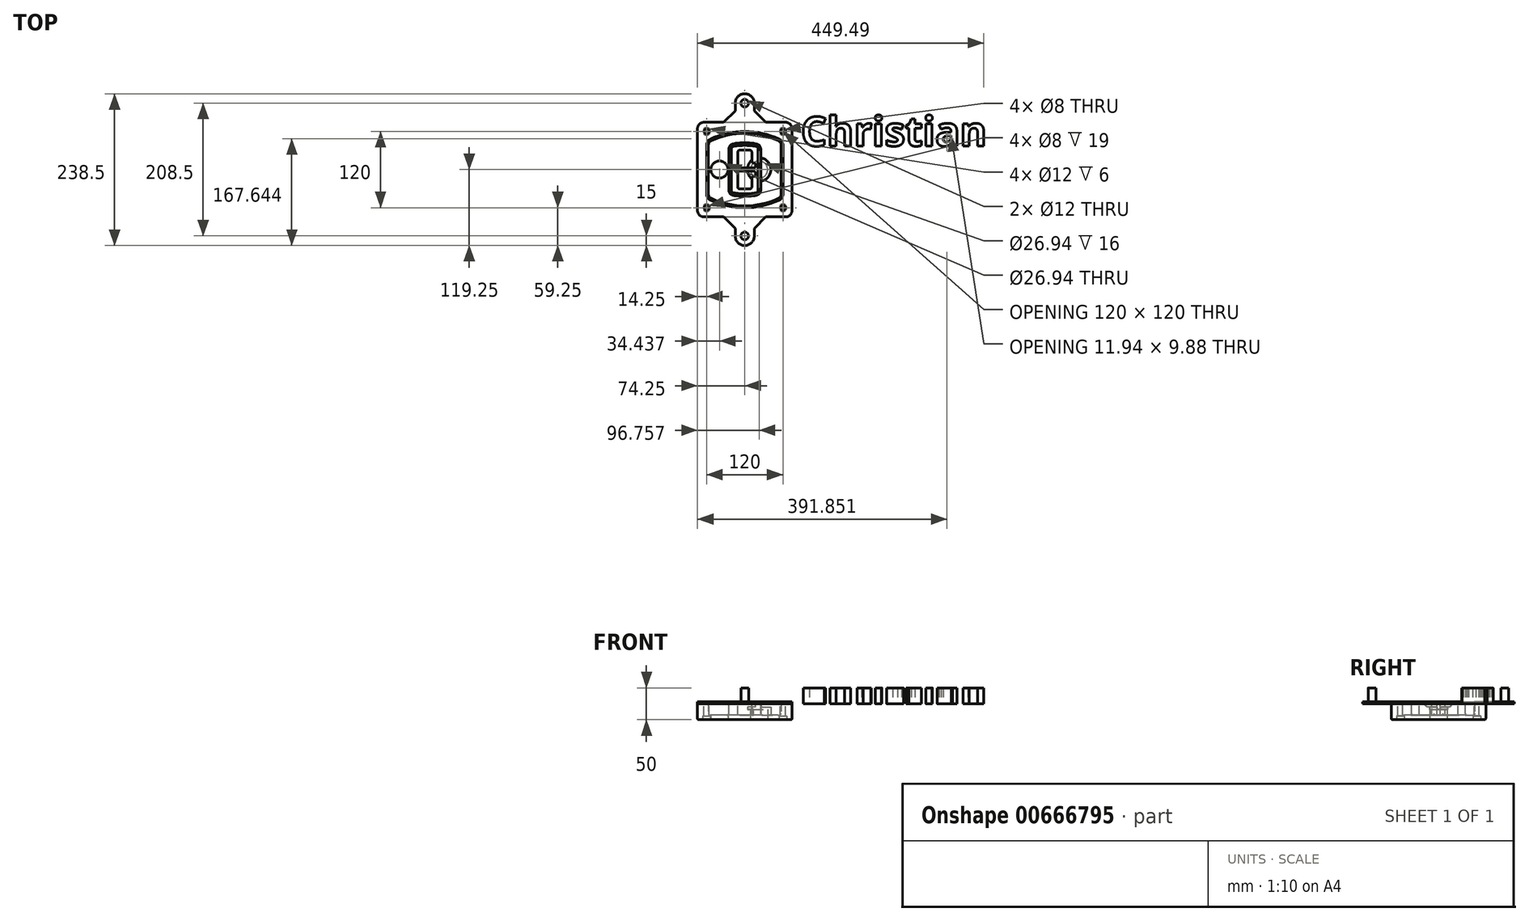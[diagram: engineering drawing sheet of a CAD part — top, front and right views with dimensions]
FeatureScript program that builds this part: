
annotation { "Feature Type Name" : "Feature", "Feature Type Description" : "" }
export const myFeature = defineFeature(function(context is Context, id is Id, definition is map)
    precondition{}
    {
        {
            var Q0;
            Q0=qCreatedBy(makeId("Top.planeOp"),FACE);
            var sketch = newSketch(context, id + "F0", { "sketchPlane" : qUnion([Q0])});
            skPoint(sketch, "E0.rect.middle", {"position": v(0, 0) * mm});
            skLineSegment(sketch, "E1.bottom", {"start": v(-64.25, -74.25) * mm, "end": v(64.25, -74.25) * mm});
            skLineSegment(sketch, "E1.top", {"start": v(-64.25, 74.25) * mm, "end": v(64.25, 74.25) * mm});
            skLineSegment(sketch, "E1.left", {"start": v(-74.25, -64.25) * mm, "end": v(-74.25, 64.25) * mm});
            skLineSegment(sketch, "E1.right", {"start": v(74.25, -64.25) * mm, "end": v(74.25, 64.25) * mm});
            skLineSegment(sketch, "E2", {"start": v(-74.25, 74.25) * mm, "end": v(74.25, -74.25) * mm, "construction": true});
            skLineSegment(sketch, "E3", {"start": v(74.25, 74.25) * mm, "end": v(-74.25, -74.25) * mm, "construction": true});
            skCircle(sketch, "E4", {"center": v(-60, 60) * mm, "radius": 4 * mm});
            skCircle(sketch, "E5", {"center": v(60, 60) * mm, "radius": 4 * mm});
            skCircle(sketch, "E6", {"center": v(60, -60) * mm, "radius": 4 * mm});
            skCircle(sketch, "E7", {"center": v(-60, -60) * mm, "radius": 4 * mm});
            skLineSegment(sketch, "E8", {"start": v(-60, 60) * mm, "end": v(60, 60) * mm, "construction": true});
            skLineSegment(sketch, "E9", {"start": v(60, 60) * mm, "end": v(60, -60) * mm, "construction": true});
            skLineSegment(sketch, "E10", {"start": v(60, -60) * mm, "end": v(-60, -60) * mm, "construction": true});
            skLineSegment(sketch, "E11", {"start": v(-60, -60) * mm, "end": v(-60, 60) * mm, "construction": true});
            skLineSegment(sketch, "E12", {"start": v(-60, 38.83) * mm, "end": v(-60, -38.83) * mm});
            skLineSegment(sketch, "E13", {"start": v(60, 38.83) * mm, "end": v(60, -38.83) * mm});
            skArc(sketch, "E14", {"start": v(54.26, 47.88) * mm, "mid": v(0, 60) * mm, "end": v(-54.26, 47.88) * mm});
            skArc(sketch, "E15", {"start": v(-54.26, -47.88) * mm, "mid": v(0, -60) * mm, "end": v(54.26, -47.88) * mm});
            skLineSegment(sketch, "E16", {"start": v(-60, 0) * mm, "end": v(60, 0) * mm, "construction": true});
            skPoint(sketch, "E17.visualSharp", {"position": v(-60, -45) * mm});
            skArc(sketch, "E17.filletArc", {"start": v(-60, -38.83) * mm, "mid": v(-58.44, -44.2) * mm, "end": v(-54.26, -47.88) * mm});
            skPoint(sketch, "E18.visualSharp", {"position": v(-60, 45) * mm});
            skArc(sketch, "E18.filletArc", {"start": v(-54.26, 47.88) * mm, "mid": v(-58.44, 44.2) * mm, "end": v(-60, 38.83) * mm});
            skPoint(sketch, "E19.visualSharp", {"position": v(60, 45) * mm});
            skArc(sketch, "E19.filletArc", {"start": v(60, 38.83) * mm, "mid": v(58.44, 44.2) * mm, "end": v(54.26, 47.88) * mm});
            skPoint(sketch, "E20.visualSharp", {"position": v(60, -45) * mm});
            skArc(sketch, "E20.filletArc", {"start": v(54.26, -47.88) * mm, "mid": v(58.44, -44.2) * mm, "end": v(60, -38.83) * mm});
            skPoint(sketch, "E21.visualSharp", {"position": v(-74.25, 74.25) * mm});
            skArc(sketch, "E21.filletArc", {"start": v(-64.25, 74.25) * mm, "mid": v(-71.32, 71.32) * mm, "end": v(-74.25, 64.25) * mm});
            skPoint(sketch, "E22.visualSharp", {"position": v(74.25, 74.25) * mm});
            skArc(sketch, "E22.filletArc", {"start": v(74.25, 64.25) * mm, "mid": v(71.32, 71.32) * mm, "end": v(64.25, 74.25) * mm});
            skPoint(sketch, "E23.visualSharp", {"position": v(74.25, -74.25) * mm});
            skArc(sketch, "E23.filletArc", {"start": v(64.25, -74.25) * mm, "mid": v(71.32, -71.32) * mm, "end": v(74.25, -64.25) * mm});
            skPoint(sketch, "E24.visualSharp", {"position": v(-74.25, -74.25) * mm});
            skArc(sketch, "E24.filletArc", {"start": v(-74.25, -64.25) * mm, "mid": v(-71.32, -71.32) * mm, "end": v(-64.25, -74.25) * mm});
            skArc(sketch, "E25.0", {"start": v(57, 38.83) * mm, "mid": v(55.9, 42.58) * mm, "end": v(52.98, 45.17) * mm});
            skLineSegment(sketch, "E25.1", {"start": v(57, 38.83) * mm, "end": v(57, -38.83) * mm});
            skArc(sketch, "E25.2", {"start": v(52.98, -45.17) * mm, "mid": v(55.9, -42.58) * mm, "end": v(57, -38.83) * mm});
            skArc(sketch, "E25.3", {"start": v(-52.98, -45.17) * mm, "mid": v(0, -57) * mm, "end": v(52.98, -45.17) * mm});
            skArc(sketch, "E25.4", {"start": v(-57, -38.83) * mm, "mid": v(-55.9, -42.58) * mm, "end": v(-52.98, -45.17) * mm});
            skArc(sketch, "E25.5", {"start": v(52.98, 45.17) * mm, "mid": v(0, 57) * mm, "end": v(-52.98, 45.17) * mm});
            skLineSegment(sketch, "E25.6", {"start": v(-57, 38.83) * mm, "end": v(-57, -38.83) * mm});
            skArc(sketch, "E25.7", {"start": v(-52.98, 45.17) * mm, "mid": v(-55.9, 42.58) * mm, "end": v(-57, 38.83) * mm});
            skArc(sketch, "E26.0", {"start": v(-55.96, 51.5) * mm, "mid": v(-61.82, 46.33) * mm, "end": v(-64, 38.83) * mm});
            skArc(sketch, "E26.1", {"start": v(55.96, 51.5) * mm, "mid": v(0, 64) * mm, "end": v(-55.96, 51.5) * mm});
            skArc(sketch, "E26.2", {"start": v(64, 38.83) * mm, "mid": v(61.82, 46.33) * mm, "end": v(55.96, 51.5) * mm});
            skLineSegment(sketch, "E26.3", {"start": v(64, 38.83) * mm, "end": v(64, -38.83) * mm});
            skArc(sketch, "E26.4", {"start": v(55.96, -51.5) * mm, "mid": v(61.82, -46.33) * mm, "end": v(64, -38.83) * mm});
            skLineSegment(sketch, "E26.5", {"start": v(-64, 38.83) * mm, "end": v(-64, -38.83) * mm});
            skArc(sketch, "E26.6", {"start": v(-55.96, -51.5) * mm, "mid": v(0, -64) * mm, "end": v(55.96, -51.5) * mm});
            skArc(sketch, "E26.7", {"start": v(-64, -38.83) * mm, "mid": v(-61.82, -46.33) * mm, "end": v(-55.96, -51.5) * mm});
            skSolve(sketch);
        }
        {
            var Q0;
            Q0=makeQuery(id+"F0.imprint","IMPRINT",FACE,{"disambiguationData":[TD([[makeQuery(id+"F0.imprint","IMPRINT",EDGE,{"derivedFrom":sQuery(id+"F0.wireOp",EDGE,"E1.bottom")}),1.0]])]});
            var Q1;
            Q1=makeQuery(id+"F0.imprint","IMPRINT",FACE,{"disambiguationData":[TD([[makeQuery(id+"F0.imprint","IMPRINT",EDGE,{"derivedFrom":sQuery(id+"F0.wireOp",EDGE,"E12")}),1.0]])]});
            var Q2;
            Q2=makeQuery(id+"F0.imprint","IMPRINT",FACE,{"disambiguationData":[TD([[makeQuery(id+"F0.imprint","IMPRINT",EDGE,{"derivedFrom":sQuery(id+"F0.wireOp",EDGE,"E25.0")}),1.0]])]});
            var Q3;
            Q3=makeQuery(id+"F0.imprint","IMPRINT",FACE,{"disambiguationData":[TD([[makeQuery(id+"F0.imprint","IMPRINT",EDGE,{"derivedFrom":sQuery(id+"F0.wireOp",EDGE,"E12")}),-1.0]])]});
            extrude(context, id + "F1", {"entities" : qUnion([Q0, Q1, Q2, Q3]), "oppositeDirection" : true, "depth" : 25 * mm});
        }
        {
            var Q0;
            Q0=makeQuery(id+"F0.imprint","IMPRINT",FACE,{"disambiguationData":[TD([[makeQuery(id+"F0.imprint","IMPRINT",EDGE,{"derivedFrom":sQuery(id+"F0.wireOp",EDGE,"E12")}),1.0]])]});
            extrude(context, id + "F2", {"entities" : qUnion([Q0]), "operationType" : NewBodyOperationType.ADD, "depth" : 3 * mm});
        }
        {
            var Q0;
            Q0=makeQuery(id+"F0.imprint","IMPRINT",FACE,{"disambiguationData":[TD([[makeQuery(id+"F0.imprint","IMPRINT",EDGE,{"derivedFrom":sQuery(id+"F0.wireOp",EDGE,"E25.0")}),1.0]])]});
            extrude(context, id + "F3", {"entities" : qUnion([Q0]), "operationType" : NewBodyOperationType.REMOVE, "oppositeDirection" : true, "depth" : 18 * mm});
        }
        {
            var Q0;
            Q0=makeQuery(id+"F2.opExtrude","CAP_FACE",FACE,{"disambiguationData":[OSD([sQuery(id+"F0.wireOp",EDGE,"E12"),sQuery(id+"F0.wireOp",EDGE,"E13"),sQuery(id+"F0.wireOp",EDGE,"E14"),sQuery(id+"F0.wireOp",EDGE,"E15"),sQuery(id+"F0.wireOp",EDGE,"E17.filletArc"),sQuery(id+"F0.wireOp",EDGE,"E18.filletArc"),sQuery(id+"F0.wireOp",EDGE,"E19.filletArc"),sQuery(id+"F0.wireOp",EDGE,"E20.filletArc"),sQuery(id+"F0.wireOp",EDGE,"E25.0"),sQuery(id+"F0.wireOp",EDGE,"E25.1"),sQuery(id+"F0.wireOp",EDGE,"E25.2"),sQuery(id+"F0.wireOp",EDGE,"E25.3"),sQuery(id+"F0.wireOp",EDGE,"E25.4"),sQuery(id+"F0.wireOp",EDGE,"E25.5"),sQuery(id+"F0.wireOp",EDGE,"E25.6"),sQuery(id+"F0.wireOp",EDGE,"E25.7")])],"isStart":false});
            var sketch = newSketch(context, id + "F4", { "sketchPlane" : qUnion([Q0])});
            skArc(sketch, "E27.0", {"start": v(-18.34, -40.45) * mm, "mid": v(0, -42) * mm, "end": v(18.34, -40.45) * mm});
            skArc(sketch, "E28.0", {"start": v(18.34, 40.45) * mm, "mid": v(0, 42) * mm, "end": v(-18.34, 40.45) * mm});
            skLineSegment(sketch, "E29", {"start": v(-25, 32.57) * mm, "end": v(-25, -32.57) * mm});
            skLineSegment(sketch, "E30", {"start": v(25, 32.57) * mm, "end": v(25, -32.57) * mm});
            skLineSegment(sketch, "E31", {"start": v(-25, 39.1) * mm, "end": v(25, 39.1) * mm, "construction": true});
            skLineSegment(sketch, "E32", {"start": v(-25, -39.1) * mm, "end": v(25, -39.1) * mm, "construction": true});
            skPoint(sketch, "E33.visualSharp", {"position": v(-25, 39.1) * mm});
            skArc(sketch, "E33.filletArc", {"start": v(-18.34, 40.45) * mm, "mid": v(-23.11, 37.73) * mm, "end": v(-25, 32.57) * mm});
            skPoint(sketch, "E34.visualSharp", {"position": v(25, 39.1) * mm});
            skArc(sketch, "E34.filletArc", {"start": v(25, 32.57) * mm, "mid": v(23.11, 37.73) * mm, "end": v(18.34, 40.45) * mm});
            skPoint(sketch, "E35.visualSharp", {"position": v(25, -39.1) * mm});
            skArc(sketch, "E35.filletArc", {"start": v(18.34, -40.45) * mm, "mid": v(23.11, -37.73) * mm, "end": v(25, -32.57) * mm});
            skPoint(sketch, "E36.visualSharp", {"position": v(-25, -39.1) * mm});
            skArc(sketch, "E36.filletArc", {"start": v(-25, -32.57) * mm, "mid": v(-23.11, -37.73) * mm, "end": v(-18.34, -40.45) * mm});
            skArc(sketch, "E37.0", {"start": v(52.98, 45.17) * mm, "mid": v(0, 57) * mm, "end": v(-52.98, 45.17) * mm});
            skArc(sketch, "E37.1", {"start": v(-52.98, 45.17) * mm, "mid": v(-55.9, 42.58) * mm, "end": v(-57, 38.83) * mm});
            skLineSegment(sketch, "E37.2", {"start": v(-57, 38.83) * mm, "end": v(-57, -38.83) * mm});
            skArc(sketch, "E37.3", {"start": v(-57, -38.83) * mm, "mid": v(-55.9, -42.58) * mm, "end": v(-52.98, -45.17) * mm});
            skArc(sketch, "E37.4", {"start": v(-52.98, -45.17) * mm, "mid": v(0, -57) * mm, "end": v(52.98, -45.17) * mm});
            skArc(sketch, "E37.5", {"start": v(52.98, -45.17) * mm, "mid": v(55.9, -42.58) * mm, "end": v(57, -38.83) * mm});
            skLineSegment(sketch, "E37.6", {"start": v(57, 38.83) * mm, "end": v(57, -38.83) * mm});
            skArc(sketch, "E37.7", {"start": v(57, 38.83) * mm, "mid": v(55.9, 42.58) * mm, "end": v(52.98, 45.17) * mm});
            skLineSegment(sketch, "E38.0", {"start": v(23, 32.57) * mm, "end": v(23, -32.57) * mm});
            skArc(sketch, "E38.1", {"start": v(18, -38.48) * mm, "mid": v(21.58, -36.44) * mm, "end": v(23, -32.57) * mm});
            skArc(sketch, "E38.2", {"start": v(-18, -38.48) * mm, "mid": v(0, -40) * mm, "end": v(18, -38.48) * mm});
            skArc(sketch, "E38.3", {"start": v(-23, -32.57) * mm, "mid": v(-21.58, -36.44) * mm, "end": v(-18, -38.48) * mm});
            skLineSegment(sketch, "E38.4", {"start": v(-23, 32.57) * mm, "end": v(-23, -32.57) * mm});
            skArc(sketch, "E38.5", {"start": v(23, 32.57) * mm, "mid": v(21.58, 36.44) * mm, "end": v(18, 38.48) * mm});
            skArc(sketch, "E38.6", {"start": v(-18, 38.48) * mm, "mid": v(-21.58, 36.44) * mm, "end": v(-23, 32.57) * mm});
            skArc(sketch, "E38.7", {"start": v(18, 38.48) * mm, "mid": v(0, 40) * mm, "end": v(-18, 38.48) * mm});
            skArc(sketch, "E39.0", {"start": v(21, 32.57) * mm, "mid": v(20.06, 35.15) * mm, "end": v(17.67, 36.5) * mm});
            skLineSegment(sketch, "E39.1", {"start": v(21, 32.57) * mm, "end": v(21, -32.57) * mm});
            skArc(sketch, "E39.2", {"start": v(17.67, -36.5) * mm, "mid": v(20.06, -35.15) * mm, "end": v(21, -32.57) * mm});
            skArc(sketch, "E39.3", {"start": v(-17.67, -36.5) * mm, "mid": v(0, -38) * mm, "end": v(17.67, -36.5) * mm});
            skArc(sketch, "E39.4", {"start": v(-21, -32.57) * mm, "mid": v(-20.06, -35.15) * mm, "end": v(-17.67, -36.5) * mm});
            skArc(sketch, "E39.5", {"start": v(17.67, 36.5) * mm, "mid": v(0, 38) * mm, "end": v(-17.67, 36.5) * mm});
            skLineSegment(sketch, "E39.6", {"start": v(-21, 32.57) * mm, "end": v(-21, -32.57) * mm});
            skArc(sketch, "E39.7", {"start": v(-17.67, 36.5) * mm, "mid": v(-20.06, 35.15) * mm, "end": v(-21, 32.57) * mm});
            skLineSegment(sketch, "E40", {"start": v(-25, 0) * mm, "end": v(25, 0) * mm, "construction": true});
            skLineSegment(sketch, "E41", {"start": v(-11, 5.5) * mm, "end": v(-11, 27.5) * mm});
            skLineSegment(sketch, "E42", {"start": v(-8, 30.5) * mm, "end": v(8, 30.5) * mm});
            skLineSegment(sketch, "E43", {"start": v(11, 27.5) * mm, "end": v(11, 13.5) * mm});
            skLineSegment(sketch, "E44", {"start": v(14, 10.5) * mm, "end": v(14, 10.5) * mm});
            skLineSegment(sketch, "E45", {"start": v(17, 7.5) * mm, "end": v(17, 5.5) * mm});
            skLineSegment(sketch, "E46", {"start": v(14, 2.5) * mm, "end": v(-8, 2.5) * mm});
            skPoint(sketch, "E47.visualSharp", {"position": v(-11, 30.5) * mm});
            skArc(sketch, "E47.filletArc", {"start": v(-8, 30.5) * mm, "mid": v(-10.12, 29.62) * mm, "end": v(-11, 27.5) * mm});
            skPoint(sketch, "E48.visualSharp", {"position": v(11, 30.5) * mm});
            skArc(sketch, "E48.filletArc", {"start": v(11, 27.5) * mm, "mid": v(10.12, 29.62) * mm, "end": v(8, 30.5) * mm});
            skPoint(sketch, "E49.visualSharp", {"position": v(11, 10.5) * mm});
            skArc(sketch, "E49.filletArc", {"start": v(11, 13.5) * mm, "mid": v(11.88, 11.38) * mm, "end": v(14, 10.5) * mm});
            skPoint(sketch, "E50.visualSharp", {"position": v(17, 10.5) * mm});
            skArc(sketch, "E50.filletArc", {"start": v(17, 7.5) * mm, "mid": v(16.12, 9.62) * mm, "end": v(14, 10.5) * mm});
            skPoint(sketch, "E51.visualSharp", {"position": v(17, 2.5) * mm});
            skArc(sketch, "E51.filletArc", {"start": v(14, 2.5) * mm, "mid": v(16.12, 3.38) * mm, "end": v(17, 5.5) * mm});
            skPoint(sketch, "E52.visualSharp", {"position": v(-11, 2.5) * mm});
            skArc(sketch, "E52.filletArc", {"start": v(-11, 5.5) * mm, "mid": v(-10.12, 3.38) * mm, "end": v(-8, 2.5) * mm});
            skLineSegment(sketch, "E53.0.MirrorCS", {"start": v(14, -2.5) * mm, "end": v(-8, -2.5) * mm});
            skArc(sketch, "E54.0.MirrorCS", {"start": v(-11, -5.5) * mm, "mid": v(-10.12, -3.38) * mm, "end": v(-8, -2.5) * mm});
            skLineSegment(sketch, "E55.0.MirrorCS", {"start": v(-11, -5.5) * mm, "end": v(-11, -27.5) * mm});
            skArc(sketch, "E56.0.MirrorCS", {"start": v(-8, -30.5) * mm, "mid": v(-10.12, -29.62) * mm, "end": v(-11, -27.5) * mm});
            skLineSegment(sketch, "E57.0.MirrorCS", {"start": v(-8, -30.5) * mm, "end": v(8, -30.5) * mm});
            skArc(sketch, "E58.0.MirrorCS", {"start": v(11, -27.5) * mm, "mid": v(10.12, -29.62) * mm, "end": v(8, -30.5) * mm});
            skLineSegment(sketch, "E59.0.MirrorCS", {"start": v(11, -27.5) * mm, "end": v(11, -13.5) * mm});
            skArc(sketch, "E60.0.MirrorCS", {"start": v(11, -13.5) * mm, "mid": v(11.88, -11.38) * mm, "end": v(14, -10.5) * mm});
            skArc(sketch, "E61.0.MirrorCS", {"start": v(17, -7.5) * mm, "mid": v(16.12, -9.62) * mm, "end": v(14, -10.5) * mm});
            skLineSegment(sketch, "E62.0.MirrorCS", {"start": v(17, -7.5) * mm, "end": v(17, -5.5) * mm});
            skArc(sketch, "E63.0.MirrorCS", {"start": v(14, -2.5) * mm, "mid": v(16.12, -3.38) * mm, "end": v(17, -5.5) * mm});
            skSolve(sketch);
        }
        {
            var Q0;
            Q0=makeQuery(id+"F4.imprint","IMPRINT",FACE,{"disambiguationData":[TD([[makeQuery(id+"F4.imprint","IMPRINT",EDGE,{"derivedFrom":sQuery(id+"F4.wireOp",EDGE,"E27.0")}),1.0]])]});
            var Q1;
            Q1=makeQuery(id+"F4.imprint","IMPRINT",FACE,{"disambiguationData":[TD([[makeQuery(id+"F4.imprint","IMPRINT",EDGE,{"derivedFrom":sQuery(id+"F4.wireOp",EDGE,"E38.0")}),-1.0]])]});
            var Q2;
            Q2=makeQuery(id+"F4.imprint","IMPRINT",FACE,{"disambiguationData":[TD([[makeQuery(id+"F4.imprint","IMPRINT",EDGE,{"derivedFrom":sQuery(id+"F4.wireOp",EDGE,"E39.0")}),1.0]])]});
            extrude(context, id + "F5", {"entities" : qUnion([Q0, Q1, Q2]), "operationType" : NewBodyOperationType.ADD, "endBound" : BoundingType.UP_TO_NEXT, "oppositeDirection" : true, "depth" : 25 * mm});
        }
        {
            var Q0;
            Q0=makeQuery(id+"F4.imprint","IMPRINT",FACE,{"disambiguationData":[TD([[makeQuery(id+"F4.imprint","IMPRINT",EDGE,{"derivedFrom":sQuery(id+"F4.wireOp",EDGE,"E38.0")}),-1.0]])]});
            extrude(context, id + "F6", {"entities" : qUnion([Q0]), "operationType" : NewBodyOperationType.REMOVE, "oppositeDirection" : true, "depth" : 2 * mm});
        }
        {
            var Q0;
            Q0=makeQuery(id+"F1.opExtrude","CAP_FACE",FACE,{"disambiguationData":[OSD([sQuery(id+"F0.wireOp",EDGE,"E1.bottom"),sQuery(id+"F0.wireOp",EDGE,"E1.top"),sQuery(id+"F0.wireOp",EDGE,"E1.left"),sQuery(id+"F0.wireOp",EDGE,"E1.right"),sQuery(id+"F0.wireOp",EDGE,"E4"),sQuery(id+"F0.wireOp",EDGE,"E5"),sQuery(id+"F0.wireOp",EDGE,"E6"),sQuery(id+"F0.wireOp",EDGE,"E7"),sQuery(id+"F0.wireOp",EDGE,"E21.filletArc"),sQuery(id+"F0.wireOp",EDGE,"E22.filletArc"),sQuery(id+"F0.wireOp",EDGE,"E23.filletArc"),sQuery(id+"F0.wireOp",EDGE,"E24.filletArc")])],"isStart":false});
            var sketch = newSketch(context, id + "F7", { "sketchPlane" : qUnion([Q0])});
            skCircle(sketch, "E64", {"center": v(22.5, 0) * mm, "radius": 13.47 * mm});
            skCircle(sketch, "E65", {"center": v(-39.81, 0) * mm, "radius": 13.47 * mm});
            skLineSegment(sketch, "E66", {"start": v(74.25, 0) * mm, "end": v(-74.25, 0) * mm});
            skCircle(sketch, "E67", {"center": v(22.5, 0) * mm, "radius": 18.47 * mm});
            skCircle(sketch, "E68", {"center": v(60, -60) * mm, "radius": 6 * mm});
            skCircle(sketch, "E69", {"center": v(-60, -60) * mm, "radius": 6 * mm});
            skCircle(sketch, "E70", {"center": v(-60, 60) * mm, "radius": 6 * mm});
            skCircle(sketch, "E71", {"center": v(60, 60) * mm, "radius": 6 * mm});
            skSolve(sketch);
        }
        {
            var Q0;
            {var subQ1=sQuery(id+"F7.wireOp",EDGE,"E66");var subQ4=sQuery(id+"F7.wireOp",EDGE,"E64");var subQ6=makeQuery(id+"F7.imprint","INTERSECT",VERTEX,{"disambiguationData":[OD(0.0)],"derivedFrom":[subQ4,subQ1]});Q0=makeQuery(id+"F7.imprint","IMPRINT",FACE,{"disambiguationData":[TD([[makeQuery(id+"F7.imprint","IMPRINT",EDGE,{"disambiguationData":[TD([[subQ6,-1.0]])],"derivedFrom":subQ4}),-1.0]])]});}
            var Q1;
            {var subQ0=sQuery(id+"F7.wireOp",EDGE,"E66");var subQ1=sQuery(id+"F7.wireOp",EDGE,"E64");var subQ3=makeQuery(id+"F7.imprint","INTERSECT",VERTEX,{"disambiguationData":[OD(0.0)],"derivedFrom":[subQ1,subQ0]});Q1=makeQuery(id+"F7.imprint","IMPRINT",FACE,{"disambiguationData":[TD([[makeQuery(id+"F7.imprint","IMPRINT",EDGE,{"disambiguationData":[TD([[subQ3,-1.0]])],"derivedFrom":subQ1}),1.0]])]});}
            var Q2;
            {var subQ0=sQuery(id+"F7.wireOp",EDGE,"E66");var subQ1=sQuery(id+"F7.wireOp",EDGE,"E64");var subQ3=makeQuery(id+"F7.imprint","INTERSECT",VERTEX,{"disambiguationData":[OD(0.0)],"derivedFrom":[subQ1,subQ0]});Q2=makeQuery(id+"F7.imprint","IMPRINT",FACE,{"disambiguationData":[TD([[makeQuery(id+"F7.imprint","IMPRINT",EDGE,{"disambiguationData":[TD([[subQ3,1.0]])],"derivedFrom":subQ1}),1.0]])]});}
            var Q3;
            {var subQ1=sQuery(id+"F7.wireOp",EDGE,"E66");var subQ4=sQuery(id+"F7.wireOp",EDGE,"E64");var subQ6=makeQuery(id+"F7.imprint","INTERSECT",VERTEX,{"disambiguationData":[OD(0.0)],"derivedFrom":[subQ4,subQ1]});Q3=makeQuery(id+"F7.imprint","IMPRINT",FACE,{"disambiguationData":[TD([[makeQuery(id+"F7.imprint","IMPRINT",EDGE,{"disambiguationData":[TD([[subQ6,1.0]])],"derivedFrom":subQ4}),-1.0]])]});}
            extrude(context, id + "F8", {"entities" : qUnion([Q0, Q1, Q2, Q3]), "operationType" : NewBodyOperationType.ADD, "oppositeDirection" : true, "depth" : 20 * mm});
        }
        {
            var Q0;
            {var subQ0=sQuery(id+"F7.wireOp",EDGE,"E66");var subQ1=sQuery(id+"F7.wireOp",EDGE,"E64");var subQ3=makeQuery(id+"F7.imprint","INTERSECT",VERTEX,{"disambiguationData":[OD(0.0)],"derivedFrom":[subQ1,subQ0]});Q0=makeQuery(id+"F7.imprint","IMPRINT",FACE,{"disambiguationData":[TD([[makeQuery(id+"F7.imprint","IMPRINT",EDGE,{"disambiguationData":[TD([[subQ3,-1.0]])],"derivedFrom":subQ1}),1.0]])]});}
            var Q1;
            {var subQ0=sQuery(id+"F7.wireOp",EDGE,"E66");var subQ1=sQuery(id+"F7.wireOp",EDGE,"E64");var subQ3=makeQuery(id+"F7.imprint","INTERSECT",VERTEX,{"disambiguationData":[OD(0.0)],"derivedFrom":[subQ1,subQ0]});Q1=makeQuery(id+"F7.imprint","IMPRINT",FACE,{"disambiguationData":[TD([[makeQuery(id+"F7.imprint","IMPRINT",EDGE,{"disambiguationData":[TD([[subQ3,1.0]])],"derivedFrom":subQ1}),1.0]])]});}
            extrude(context, id + "F9", {"entities" : qUnion([Q0, Q1]), "operationType" : NewBodyOperationType.REMOVE, "oppositeDirection" : true, "depth" : 16 * mm});
        }
        {
            var Q0;
            {var subQ0=sQuery(id+"F7.wireOp",EDGE,"E66");var subQ1=sQuery(id+"F7.wireOp",EDGE,"E65");var subQ3=makeQuery(id+"F7.imprint","INTERSECT",VERTEX,{"disambiguationData":[OD(0.0)],"derivedFrom":[subQ1,subQ0]});Q0=makeQuery(id+"F7.imprint","IMPRINT",FACE,{"disambiguationData":[TD([[makeQuery(id+"F7.imprint","IMPRINT",EDGE,{"disambiguationData":[TD([[subQ3,-1.0]])],"derivedFrom":subQ1}),1.0]])]});}
            var Q1;
            {var subQ0=sQuery(id+"F7.wireOp",EDGE,"E66");var subQ1=sQuery(id+"F7.wireOp",EDGE,"E65");var subQ3=makeQuery(id+"F7.imprint","INTERSECT",VERTEX,{"disambiguationData":[OD(0.0)],"derivedFrom":[subQ1,subQ0]});Q1=makeQuery(id+"F7.imprint","IMPRINT",FACE,{"disambiguationData":[TD([[makeQuery(id+"F7.imprint","IMPRINT",EDGE,{"disambiguationData":[TD([[subQ3,1.0]])],"derivedFrom":subQ1}),1.0]])]});}
            extrude(context, id + "F10", {"entities" : qUnion([Q0, Q1]), "operationType" : NewBodyOperationType.REMOVE, "oppositeDirection" : true, "depth" : 25 * mm});
        }
        {
            var Q0;
            Q0=makeQuery(id+"F7.imprint","IMPRINT",FACE,{"disambiguationData":[TD([[makeQuery(id+"F7.imprint","IMPRINT",EDGE,{"derivedFrom":sQuery(id+"F7.wireOp",EDGE,"E68")}),1.0]])]});
            var Q1;
            Q1=makeQuery(id+"F7.imprint","IMPRINT",FACE,{"disambiguationData":[TD([[makeQuery(id+"F7.imprint","IMPRINT",EDGE,{"derivedFrom":makeQuery(id+"F1.opExtrude","CAP_EDGE",EDGE,{"disambiguationData":[OSD([sQuery(id+"F0.wireOp",EDGE,"E5")])],"isStart":false})}),-1.0]])]});
            var Q2;
            Q2=makeQuery(id+"F7.imprint","IMPRINT",FACE,{"disambiguationData":[TD([[makeQuery(id+"F7.imprint","IMPRINT",EDGE,{"derivedFrom":sQuery(id+"F7.wireOp",EDGE,"E69")}),1.0]])]});
            var Q3;
            Q3=makeQuery(id+"F7.imprint","IMPRINT",FACE,{"disambiguationData":[TD([[makeQuery(id+"F7.imprint","IMPRINT",EDGE,{"derivedFrom":makeQuery(id+"F1.opExtrude","CAP_EDGE",EDGE,{"disambiguationData":[OSD([sQuery(id+"F0.wireOp",EDGE,"E4")])],"isStart":false})}),-1.0]])]});
            var Q4;
            Q4=makeQuery(id+"F7.imprint","IMPRINT",FACE,{"disambiguationData":[TD([[makeQuery(id+"F7.imprint","IMPRINT",EDGE,{"derivedFrom":sQuery(id+"F7.wireOp",EDGE,"E70")}),1.0]])]});
            var Q5;
            Q5=makeQuery(id+"F7.imprint","IMPRINT",FACE,{"disambiguationData":[TD([[makeQuery(id+"F7.imprint","IMPRINT",EDGE,{"derivedFrom":makeQuery(id+"F1.opExtrude","CAP_EDGE",EDGE,{"disambiguationData":[OSD([sQuery(id+"F0.wireOp",EDGE,"E7")])],"isStart":false})}),-1.0]])]});
            var Q6;
            Q6=makeQuery(id+"F7.imprint","IMPRINT",FACE,{"disambiguationData":[TD([[makeQuery(id+"F7.imprint","IMPRINT",EDGE,{"derivedFrom":sQuery(id+"F7.wireOp",EDGE,"E71")}),1.0]])]});
            var Q7;
            Q7=makeQuery(id+"F7.imprint","IMPRINT",FACE,{"disambiguationData":[TD([[makeQuery(id+"F7.imprint","IMPRINT",EDGE,{"derivedFrom":makeQuery(id+"F1.opExtrude","CAP_EDGE",EDGE,{"disambiguationData":[OSD([sQuery(id+"F0.wireOp",EDGE,"E6")])],"isStart":false})}),-1.0]])]});
            extrude(context, id + "F11", {"entities" : qUnion([Q0, Q1, Q2, Q3, Q4, Q5, Q6, Q7]), "operationType" : NewBodyOperationType.REMOVE, "oppositeDirection" : true, "depth" : 6 * mm});
        }
        {
            var Q0;
            Q0=makeQuery(id+"F9.boolean.opBoolean","COPY",FACE,{"derivedFrom":makeQuery(id+"F9.opExtrude","CAP_FACE",FACE,{"disambiguationData":[OSD([sQuery(id+"F7.wireOp",EDGE,"E64")])],"isStart":false})});
            var sketch = newSketch(context, id + "F12", { "sketchPlane" : qUnion([Q0])});
            skArc(sketch, "E72.0", {"start": v(11, 14.45) * mm, "mid": v(6.45, 9.13) * mm, "end": v(4.2, 2.5) * mm});
            skArc(sketch, "E72.1", {"start": v(4.2, -2.5) * mm, "mid": v(6.45, -9.13) * mm, "end": v(11, -14.45) * mm});
            skLineSegment(sketch, "E73", {"start": v(4.2, -2.5) * mm, "end": v(14, -2.5) * mm});
            skLineSegment(sketch, "E74.0", {"start": v(14, 2.5) * mm, "end": v(4.2, 2.5) * mm});
            skArc(sketch, "E74.1", {"start": v(14, 2.5) * mm, "mid": v(16.12, 3.38) * mm, "end": v(17, 5.5) * mm});
            skLineSegment(sketch, "E74.2", {"start": v(17, 7.5) * mm, "end": v(17, 5.5) * mm});
            skArc(sketch, "E74.3", {"start": v(17, 7.5) * mm, "mid": v(16.12, 9.62) * mm, "end": v(14, 10.5) * mm});
            skArc(sketch, "E74.4", {"start": v(11, 13.5) * mm, "mid": v(11.88, 11.38) * mm, "end": v(14, 10.5) * mm});
            skLineSegment(sketch, "E74.5", {"start": v(11, 14.45) * mm, "end": v(11, 13.5) * mm});
            skLineSegment(sketch, "E74.7", {"start": v(14, -2.5) * mm, "end": v(4.2, -2.5) * mm});
            skArc(sketch, "E74.8", {"start": v(14, -2.5) * mm, "mid": v(16.12, -3.38) * mm, "end": v(17, -5.5) * mm});
            skLineSegment(sketch, "E74.9", {"start": v(17, -7.5) * mm, "end": v(17, -5.5) * mm});
            skArc(sketch, "E74.10", {"start": v(17, -7.5) * mm, "mid": v(16.12, -9.62) * mm, "end": v(14, -10.5) * mm});
            skArc(sketch, "E74.11", {"start": v(11, -13.5) * mm, "mid": v(11.88, -11.38) * mm, "end": v(14, -10.5) * mm});
            skLineSegment(sketch, "E74.12", {"start": v(11, -14.45) * mm, "end": v(11, -13.5) * mm});
            skPoint(sketch, "E75.orphan", {"position": v(11, -27.5) * mm});
            skPoint(sketch, "E76.orphan", {"position": v(-8, -2.5) * mm});
            skPoint(sketch, "E77.orphan", {"position": v(-8, 2.5) * mm});
            skPoint(sketch, "E78.orphan", {"position": v(11, 27.5) * mm});
            skSolve(sketch);
        }
        {
            var Q0;
            {var subQ7=sQuery(id+"F12.wireOp",EDGE,"E72.0");var subQ14=sQuery(id+"F12.wireOp",EDGE,"E72.1");var subQ16=sQuery(id+"F12.wireOp",EDGE,"E74.1");var subQ18=sQuery(id+"F12.wireOp",EDGE,"E74.8");Q0=qUnion([makeQuery(id+"F12.imprint","IMPRINT",FACE,{"disambiguationData":[TD([[makeQuery(id+"F12.imprint","IMPRINT",EDGE,{"derivedFrom":subQ7}),1.0]])]}),makeQuery(id+"F12.imprint","IMPRINT",FACE,{"disambiguationData":[TD([[makeQuery(id+"F12.imprint","IMPRINT",EDGE,{"derivedFrom":subQ14}),1.0]])]}),makeQuery(id+"F12.imprint","IMPRINT",FACE,{"disambiguationData":[TD([[makeQuery(id+"F12.imprint","IMPRINT",EDGE,{"derivedFrom":subQ16}),1.0]])]}),makeQuery(id+"F12.imprint","IMPRINT",FACE,{"disambiguationData":[TD([[makeQuery(id+"F12.imprint","IMPRINT",EDGE,{"derivedFrom":subQ18}),-1.0]])]})]);}
            var Q1;
            Q1=makeQuery(id+"F5.boolean.opBoolean","SPLIT",FACE,{"disambiguationData":[TD([makeQuery(id+"F5.opExtrude","SWEPT_FACE",FACE,{"disambiguationData":[OSD([sQuery(id+"F4.wireOp",EDGE,"E41")])]})])],"derivedFrom":makeQuery(id+"F3.boolean.opBoolean","COPY",FACE,{"derivedFrom":makeQuery(id+"F3.opExtrude","CAP_FACE",FACE,{"disambiguationData":[OSD([sQuery(id+"F0.wireOp",EDGE,"E25.0"),sQuery(id+"F0.wireOp",EDGE,"E25.1"),sQuery(id+"F0.wireOp",EDGE,"E25.2"),sQuery(id+"F0.wireOp",EDGE,"E25.3"),sQuery(id+"F0.wireOp",EDGE,"E25.4"),sQuery(id+"F0.wireOp",EDGE,"E25.5"),sQuery(id+"F0.wireOp",EDGE,"E25.6"),sQuery(id+"F0.wireOp",EDGE,"E25.7")])],"isStart":false})})});
            extrude(context, id + "F13", {"entities" : qUnion([Q0]), "operationType" : NewBodyOperationType.REMOVE, "endBound" : BoundingType.UP_TO_SURFACE, "endBoundEntityFace" : qUnion([Q1]), "depth" : 25 * mm});
        }
        {
            var Q0;
            Q0=makeQuery(id+"F3.boolean.opBoolean","COPY",EDGE,{"derivedFrom":makeQuery(id+"F3.opExtrude","CAP_EDGE",EDGE,{"disambiguationData":[OSD([sQuery(id+"F0.wireOp",EDGE,"E25.6")])],"isStart":false})});
            var Q1;
            Q1=makeQuery(id+"F8.boolean.opBoolean","INTERSECT",EDGE,{"derivedFrom":[makeQuery(id+"F5.opExtrude","SWEPT_FACE",FACE,{"disambiguationData":[OSD([sQuery(id+"F4.wireOp",EDGE,"E30")])]}),makeQuery(id+"F8.opExtrude","CAP_FACE",FACE,{"disambiguationData":[OSD([sQuery(id+"F7.wireOp",EDGE,"E67")])],"isStart":false})]});
            var Q2;
            Q2=makeQuery(id+"F8.boolean.opBoolean","INTERSECT",EDGE,{"disambiguationData":[OD(1.0)],"derivedFrom":[makeQuery(id+"F5.opExtrude","SWEPT_FACE",FACE,{"disambiguationData":[OSD([sQuery(id+"F4.wireOp",EDGE,"E30")])]}),makeQuery(id+"F8.opExtrude","SWEPT_FACE",FACE,{"disambiguationData":[OSD([sQuery(id+"F7.wireOp",EDGE,"E67")])]})]});
            var Q3;
            {var subQ0=sQuery(id+"F4.wireOp",EDGE,"E30");Q3=makeQuery(id+"F8.boolean.opBoolean","SPLIT",EDGE,{"disambiguationData":[TD([makeQuery(id+"F5.opExtrude","SWEPT_FACE",FACE,{"disambiguationData":[OSD([sQuery(id+"F4.wireOp",EDGE,"E35.filletArc")])]})])],"derivedFrom":makeQuery(id+"F5.opExtrude","CAP_EDGE",EDGE,{"disambiguationData":[OSD([subQ0])],"isStart":false})});}
            var Q4;
            {var subQ0=sQuery(id+"F0.wireOp",EDGE,"E25.7");var subQ1=sQuery(id+"F0.wireOp",EDGE,"E25.1");var subQ2=sQuery(id+"F0.wireOp",EDGE,"E25.6");var subQ3=sQuery(id+"F0.wireOp",EDGE,"E25.5");var subQ4=sQuery(id+"F0.wireOp",EDGE,"E25.4");var subQ5=sQuery(id+"F0.wireOp",EDGE,"E25.0");var subQ6=sQuery(id+"F0.wireOp",EDGE,"E25.2");var subQ7=sQuery(id+"F0.wireOp",EDGE,"E25.3");Q4=makeQuery(id+"F8.boolean.opBoolean","INTERSECT",EDGE,{"derivedFrom":[makeQuery(id+"F5.boolean.opBoolean","SPLIT",FACE,{"disambiguationData":[TD([makeQuery(id+"F2.opExtrude","SWEPT_FACE",FACE,{"disambiguationData":[OSD([subQ5])]})])],"derivedFrom":makeQuery(id+"F3.boolean.opBoolean","COPY",FACE,{"derivedFrom":makeQuery(id+"F3.opExtrude","CAP_FACE",FACE,{"disambiguationData":[OSD([subQ5,subQ1,subQ6,subQ7,subQ4,subQ3,subQ2,subQ0])],"isStart":false})})}),makeQuery(id+"F8.opExtrude","SWEPT_FACE",FACE,{"disambiguationData":[OSD([sQuery(id+"F7.wireOp",EDGE,"E67")])]})]});}
            var Q5;
            Q5=makeQuery(id+"F8.boolean.opBoolean","INTERSECT",EDGE,{"disambiguationData":[OD(0.0)],"derivedFrom":[makeQuery(id+"F5.opExtrude","SWEPT_FACE",FACE,{"disambiguationData":[OSD([sQuery(id+"F4.wireOp",EDGE,"E30")])]}),makeQuery(id+"F8.opExtrude","SWEPT_FACE",FACE,{"disambiguationData":[OSD([sQuery(id+"F7.wireOp",EDGE,"E67")])]})]});
            fillet(context, id + "F14", {"entities" : qUnion([Q0, Q1, Q2, Q3, Q4, Q5]), "radius" : 3 * mm, "tangentPropagation" : true, "allowEdgeOverflow" : false});
        }
        {
            var Q0;
            Q0=makeQuery(id+"F1.opExtrude","CAP_EDGE",EDGE,{"disambiguationData":[OSD([sQuery(id+"F0.wireOp",EDGE,"E1.bottom")])],"isStart":false});
            fillet(context, id + "F15", {"entities" : qUnion([Q0]), "radius" : 2 * mm, "tangentPropagation" : true, "allowEdgeOverflow" : false});
        }
        {
            var Q0;
            {var subQ0=sQuery(id+"F0.wireOp",EDGE,"E21.filletArc");var subQ1=sQuery(id+"F0.wireOp",EDGE,"E7");var subQ2=sQuery(id+"F0.wireOp",EDGE,"E6");var subQ3=sQuery(id+"F0.wireOp",EDGE,"E5");var subQ4=sQuery(id+"F0.wireOp",EDGE,"E4");var subQ5=sQuery(id+"F0.wireOp",EDGE,"E22.filletArc");var subQ6=sQuery(id+"F0.wireOp",EDGE,"E1.bottom");var subQ7=sQuery(id+"F0.wireOp",EDGE,"E1.right");var subQ8=sQuery(id+"F0.wireOp",EDGE,"E1.top");var subQ9=sQuery(id+"F0.wireOp",EDGE,"E1.left");var subQ10=sQuery(id+"F0.wireOp",EDGE,"E23.filletArc");var subQ11=sQuery(id+"F0.wireOp",EDGE,"E24.filletArc");Q0=makeQuery(id+"F2.boolean.opBoolean","SPLIT",FACE,{"disambiguationData":[TD([makeQuery(id+"F1.opExtrude","SWEPT_FACE",FACE,{"disambiguationData":[OSD([subQ6])]})])],"derivedFrom":makeQuery(id+"F1.opExtrude","CAP_FACE",FACE,{"disambiguationData":[OSD([subQ6,subQ8,subQ9,subQ7,subQ4,subQ3,subQ2,subQ1,subQ0,subQ5,subQ10,subQ11])],"isStart":true})});}
            var sketch = newSketch(context, id + "F16", { "sketchPlane" : qUnion([Q0])});
            skCircle(sketch, "E79", {"center": v(0, 104.25) * mm, "radius": 6 * mm});
            skArc(sketch, "E80", {"start": v(-15, 104.25) * mm, "mid": v(0, 119.25) * mm, "end": v(15, 104.25) * mm});
            skLineSegment(sketch, "E81", {"start": v(-15, 92.25) * mm, "end": v(-33, 74.25) * mm});
            skLineSegment(sketch, "E82", {"start": v(-15, 104.25) * mm, "end": v(-15, 92.25) * mm});
            skLineSegment(sketch, "E83", {"start": v(15, 92.25) * mm, "end": v(33, 74.25) * mm});
            skLineSegment(sketch, "E84", {"start": v(15, 104.25) * mm, "end": v(15, 92.25) * mm});
            skLineSegment(sketch, "E85", {"start": v(-74.25, 0) * mm, "end": v(74.25, 0) * mm, "construction": true});
            skLineSegment(sketch, "E86.MirrorCS", {"start": v(15, -92.25) * mm, "end": v(33, -74.25) * mm});
            skLineSegment(sketch, "E87.MirrorCS", {"start": v(15, -104.25) * mm, "end": v(15, -92.25) * mm});
            skArc(sketch, "E88.MirrorCS", {"start": v(-15, -104.25) * mm, "mid": v(0, -119.25) * mm, "end": v(15, -104.25) * mm});
            skCircle(sketch, "E89.MirrorC", {"center": v(0, -104.25) * mm, "radius": 6 * mm});
            skLineSegment(sketch, "E90.MirrorCS", {"start": v(-15, -104.25) * mm, "end": v(-15, -92.25) * mm});
            skLineSegment(sketch, "E91.MirrorCS", {"start": v(-15, -92.25) * mm, "end": v(-33, -74.25) * mm});
            skText(sketch, "E92", { "text": "Christian", "fontName": "OpenSans-Bold.ttf"});
            const initialGuessF16  = {"E92": [0.08803, 0.0371, 1, 0, 0.0462]};
            skSetInitialGuess(sketch, initialGuessF16);
            skSolve(sketch);
        }
        {
            var Q0;
            Q0 = qSketchRegion(id + "F16", true);
            extrude(context, id + "F17", {"entities" : qUnion([Q0]), "depth" : 25 * mm, "offsetDistance" : 25 * mm});
        }
        {
            var Q0;
            Q0=makeQuery(id+"F16.imprint","IMPRINT",FACE,{"disambiguationData":[TD([[makeQuery(id+"F16.imprint","IMPRINT",EDGE,{"derivedFrom":sQuery(id+"F16.wireOp",EDGE,"E79")}),-1.0]])]});
            var Q1;
            Q1=makeQuery(id+"F16.imprint","IMPRINT",FACE,{"disambiguationData":[TD([[makeQuery(id+"F16.imprint","IMPRINT",EDGE,{"derivedFrom":makeQuery(id+"F1.opExtrude","CAP_EDGE",EDGE,{"disambiguationData":[OSD([sQuery(id+"F0.wireOp",EDGE,"E1.left")])],"isStart":true})}),-1.0]])]});
            var Q2;
            {var subQ0=sQuery(id+"F16.wireOp",EDGE,"E86.MirrorCS");Q2=makeQuery(id+"F16.imprint","IMPRINT",FACE,{"disambiguationData":[TD([[makeQuery(id+"F16.imprint","IMPRINT",EDGE,{"derivedFrom":subQ0}),1.0]])]});}
            var Q3;
            Q3=makeQuery(id+"F2.opExtrude","CAP_FACE",FACE,{"disambiguationData":[OSD([sQuery(id+"F0.wireOp",EDGE,"E12"),sQuery(id+"F0.wireOp",EDGE,"E13"),sQuery(id+"F0.wireOp",EDGE,"E14"),sQuery(id+"F0.wireOp",EDGE,"E15"),sQuery(id+"F0.wireOp",EDGE,"E17.filletArc"),sQuery(id+"F0.wireOp",EDGE,"E18.filletArc"),sQuery(id+"F0.wireOp",EDGE,"E19.filletArc"),sQuery(id+"F0.wireOp",EDGE,"E20.filletArc"),sQuery(id+"F0.wireOp",EDGE,"E25.0"),sQuery(id+"F0.wireOp",EDGE,"E25.1"),sQuery(id+"F0.wireOp",EDGE,"E25.2"),sQuery(id+"F0.wireOp",EDGE,"E25.3"),sQuery(id+"F0.wireOp",EDGE,"E25.4"),sQuery(id+"F0.wireOp",EDGE,"E25.5"),sQuery(id+"F0.wireOp",EDGE,"E25.6"),sQuery(id+"F0.wireOp",EDGE,"E25.7")])],"isStart":false});
            extrude(context, id + "F18", {"entities" : qUnion([Q0, Q1, Q2]), "endBound" : BoundingType.UP_TO_SURFACE, "depth" : 25 * mm, "endBoundEntityFace" : qUnion([Q3]), "offsetDistance" : 25 * mm});
        }
    });
